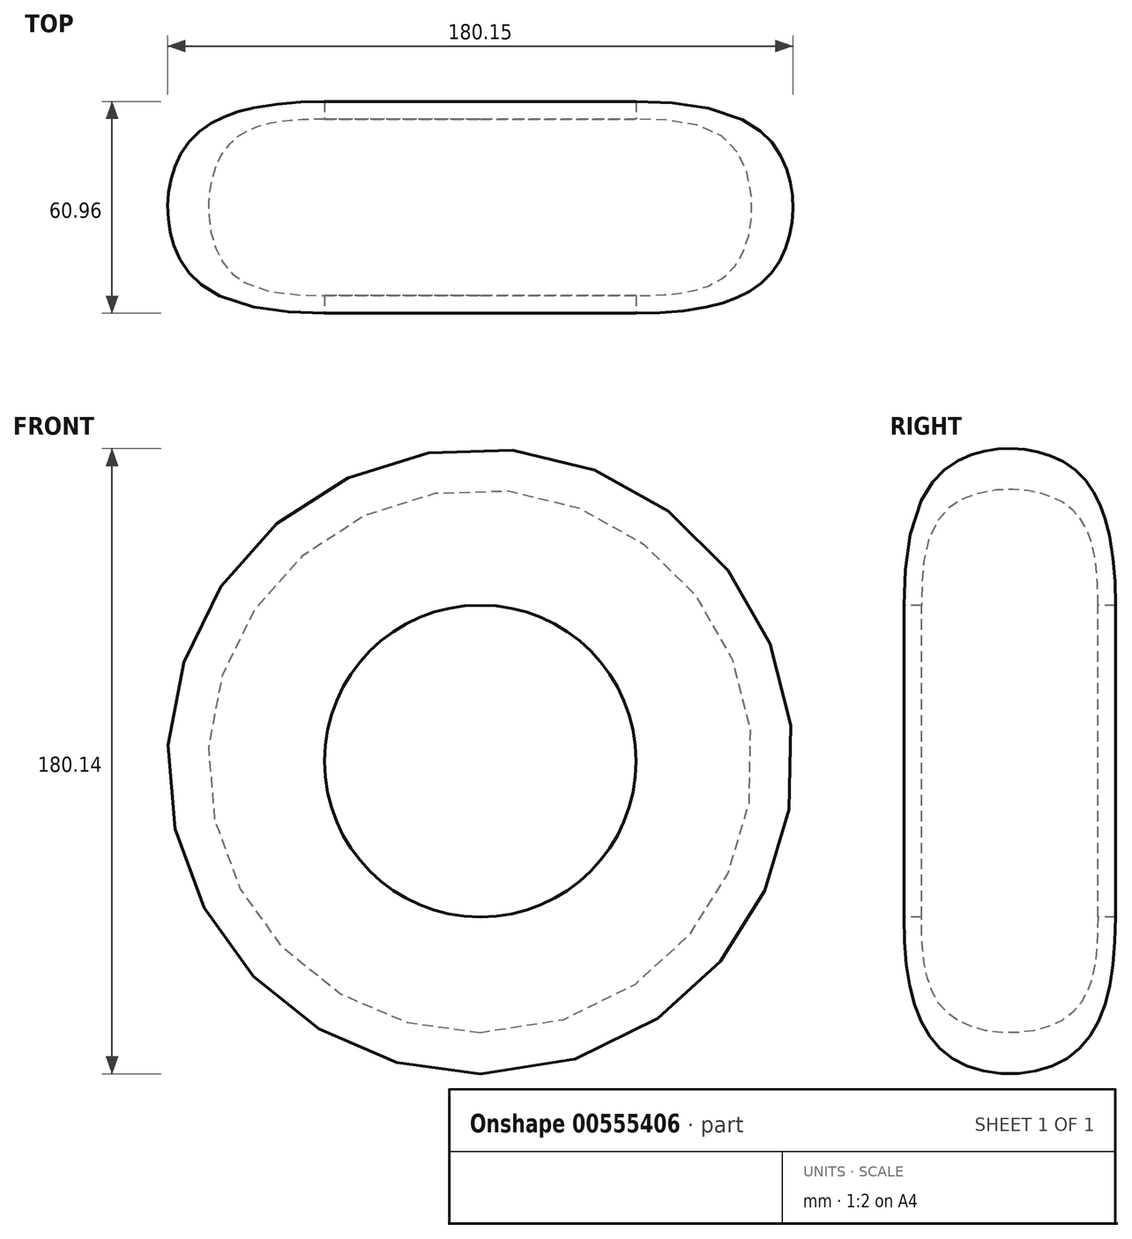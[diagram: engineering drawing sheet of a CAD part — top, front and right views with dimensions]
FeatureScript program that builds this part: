
annotation { "Feature Type Name" : "Feature", "Feature Type Description" : "" }
export const myFeature = defineFeature(function(context is Context, id is Id, definition is map)
    precondition{}
    {
        {
            var Q0;
            Q0=qCreatedBy(makeId("Top.planeOp"),FACE);
            var sketch = newSketch(context, id + "F0", { "sketchPlane" : qUnion([Q0])});
            skFitSpline(sketch, "E0", {"points": [v(0, 30.48) * mm, v(-40.75, 16.51) * mm, v(-40.75, -16.51) * mm, v(0, -30.48) * mm], "startDerivative": vector(-169.74, 0) * mm, "endDerivative": vector(169.74, 0) * mm});
            skFitSpline(sketch, "E1", {"points": [v(0, 25.4) * mm, v(-28.81, 16.51) * mm, v(-28.81, -16.51) * mm, v(0, -25.4) * mm], "startDerivative": vector(-106.7, 0) * mm, "endDerivative": vector(106.7, 0) * mm});
            skLineSegment(sketch, "E2", {"start": v(0, 30.48) * mm, "end": v(0, 25.4) * mm});
            skLineSegment(sketch, "E3", {"start": v(0, -25.4) * mm, "end": v(0, -30.48) * mm});
            skLineSegment(sketch, "E4", {"start": v(44.93, 0) * mm, "end": v(44.93, 20.54) * mm});
            skSolve(sketch);
        }
        {
            var Q0;
            Q0=makeQuery(id+"F0.imprint","IMPRINT",FACE,{"disambiguationData":[TD([[makeQuery(id+"F0.imprint","IMPRINT",EDGE,{"derivedFrom":sQuery(id+"F0.wireOp",EDGE,"E0")}),1.0]])]});
            var Q1;
            Q1=sQuery(id+"F0.wireOp",EDGE,"E4");
            revolve(context, id + "F1", {"entities" : qUnion([Q0]), "axis" : qUnion([Q1]), "revolveType" : RevolveType.FULL});
        }
    });
